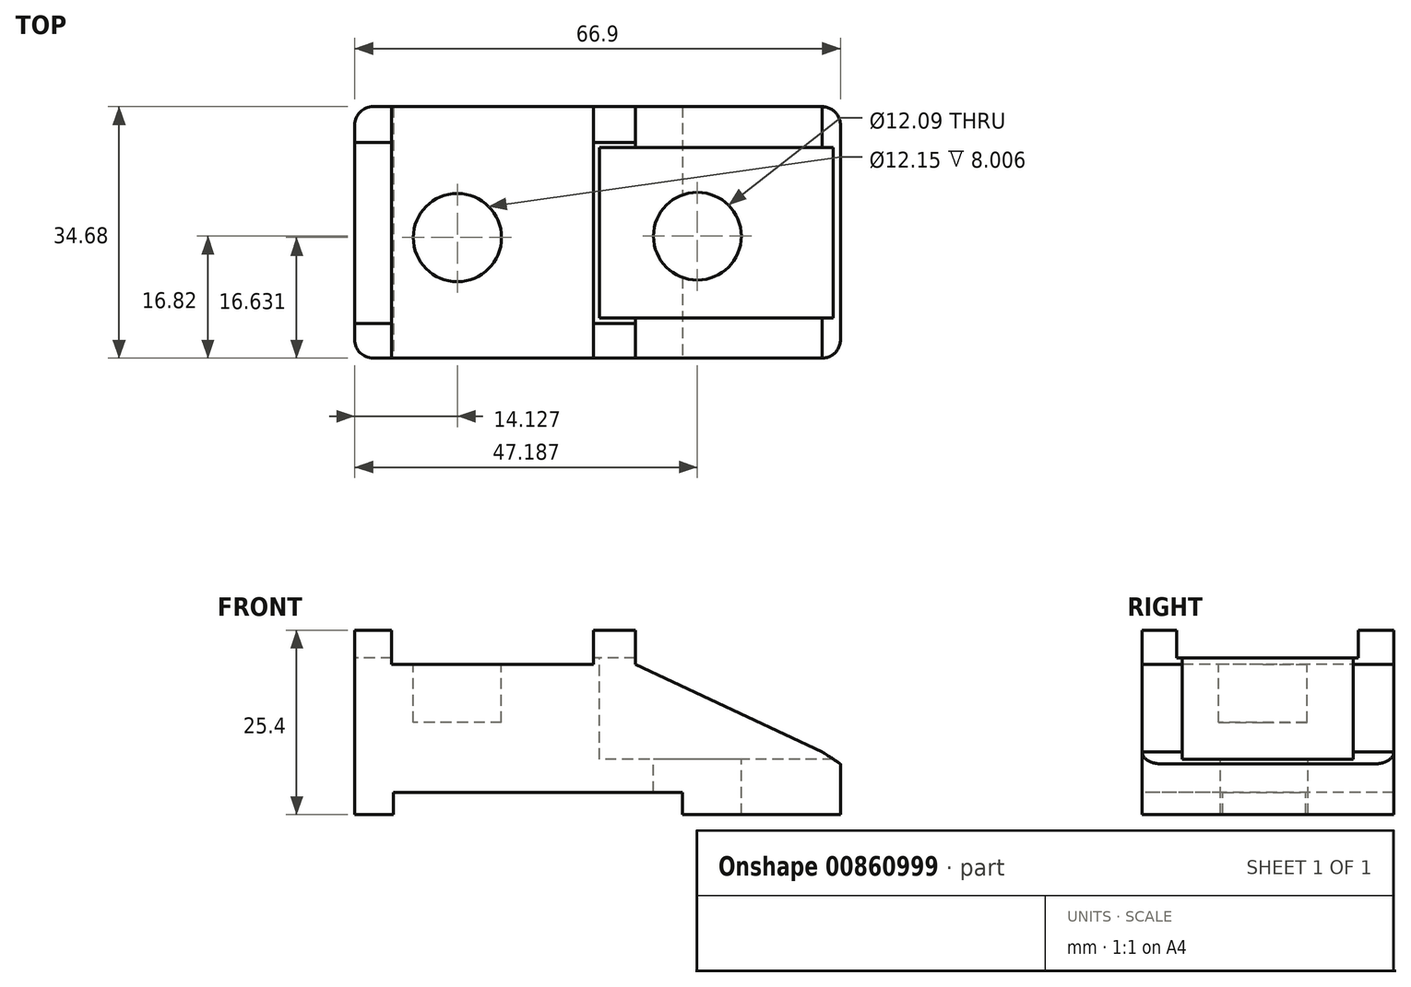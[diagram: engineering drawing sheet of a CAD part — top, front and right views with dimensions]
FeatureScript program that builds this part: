
annotation { "Feature Type Name" : "Feature", "Feature Type Description" : "" }
export const myFeature = defineFeature(function(context is Context, id is Id, definition is map)
    precondition{}
    {
        {
            var Q0;
            Q0=qCreatedBy(makeId("Top.planeOp"),FACE);
            var sketch = newSketch(context, id + "F0", { "sketchPlane" : qUnion([Q0])});
            skLineSegment(sketch, "E0.bottom", {"start": v(0, 0) * mm, "end": v(66.9, 0) * mm});
            skLineSegment(sketch, "E0.top", {"start": v(0, 34.68) * mm, "end": v(66.9, 34.68) * mm});
            skLineSegment(sketch, "E0.left", {"start": v(0, 0) * mm, "end": v(0, 34.68) * mm});
            skLineSegment(sketch, "E0.right", {"start": v(66.9, 0) * mm, "end": v(66.9, 34.68) * mm});
            skSolve(sketch);
        }
        {
            var Q0;
            Q0=makeQuery(id+"F0.imprint","IMPRINT",FACE,{"disambiguationData":[TD([[makeQuery(id+"F0.imprint","IMPRINT",EDGE,{"derivedFrom":sQuery(id+"F0.wireOp",EDGE,"E0.bottom")}),1.0]])]});
            extrude(context, id + "F1", {"entities" : qUnion([Q0]), "depth" : 25.4 * mm, "offsetDistance" : 25.4 * mm});
        }
        {
            var Q0;
            Q0=makeQuery(id+"F1.opExtrude","CAP_FACE",FACE,{"disambiguationData":[OSD([sQuery(id+"F0.wireOp",EDGE,"E0.bottom"),sQuery(id+"F0.wireOp",EDGE,"E0.top"),sQuery(id+"F0.wireOp",EDGE,"E0.left"),sQuery(id+"F0.wireOp",EDGE,"E0.right")])],"isStart":false});
            var sketch = newSketch(context, id + "F2", { "sketchPlane" : qUnion([Q0])});
            skCircle(sketch, "E1", {"center": v(47.19, 16.82) * mm, "radius": 6.05 * mm});
            skSolve(sketch);
        }
        {
            var Q0;
            Q0=makeQuery(id+"F2.imprint","IMPRINT",FACE,{"disambiguationData":[TD([[makeQuery(id+"F2.imprint","IMPRINT",EDGE,{"derivedFrom":sQuery(id+"F2.wireOp",EDGE,"E1")}),1.0]])]});
            extrude(context, id + "F3", {"entities" : qUnion([Q0]), "operationType" : NewBodyOperationType.REMOVE, "endBound" : BoundingType.THROUGH_ALL, "oppositeDirection" : true, "depth" : 25.4 * mm, "offsetDistance" : 25.4 * mm});
        }
        {
            var Q0;
            Q0=makeQuery(id+"F1.opExtrude","CAP_FACE",FACE,{"disambiguationData":[OSD([sQuery(id+"F0.wireOp",EDGE,"E0.bottom"),sQuery(id+"F0.wireOp",EDGE,"E0.top"),sQuery(id+"F0.wireOp",EDGE,"E0.left"),sQuery(id+"F0.wireOp",EDGE,"E0.right")])],"isStart":false});
            var sketch = newSketch(context, id + "F4", { "sketchPlane" : qUnion([Q0])});
            skCircle(sketch, "E2", {"center": v(14.13, 16.63) * mm, "radius": 6.08 * mm});
            skSolve(sketch);
        }
        {
            var Q0;
            Q0=makeQuery(id+"F4.imprint","IMPRINT",FACE,{"disambiguationData":[TD([[makeQuery(id+"F4.imprint","IMPRINT",EDGE,{"derivedFrom":sQuery(id+"F4.wireOp",EDGE,"E2")}),1.0]])]});
            extrude(context, id + "F5", {"entities" : qUnion([Q0]), "operationType" : NewBodyOperationType.REMOVE, "oppositeDirection" : true, "depth" : 12.7 * mm, "offsetDistance" : 25.4 * mm});
        }
        {
            var Q0;
            Q0=makeQuery(id+"F1.opExtrude","CAP_FACE",FACE,{"disambiguationData":[OSD([sQuery(id+"F0.wireOp",EDGE,"E0.bottom"),sQuery(id+"F0.wireOp",EDGE,"E0.top"),sQuery(id+"F0.wireOp",EDGE,"E0.left"),sQuery(id+"F0.wireOp",EDGE,"E0.right")])],"isStart":false});
            var sketch = newSketch(context, id + "F6", { "sketchPlane" : qUnion([Q0])});
            skLineSegment(sketch, "E3.bottom", {"start": v(66.9, 29.05) * mm, "end": v(33.67, 29.05) * mm});
            skLineSegment(sketch, "E3.top", {"start": v(66.9, 5.54) * mm, "end": v(33.67, 5.54) * mm});
            skLineSegment(sketch, "E3.left", {"start": v(66.9, 29.05) * mm, "end": v(66.9, 5.54) * mm});
            skLineSegment(sketch, "E3.right", {"start": v(33.67, 29.05) * mm, "end": v(33.67, 5.54) * mm});
            skSolve(sketch);
        }
        {
            var Q0;
            Q0=makeQuery(id+"F6.imprint","IMPRINT",FACE,{"disambiguationData":[TD([[makeQuery(id+"F6.imprint","IMPRINT",EDGE,{"derivedFrom":sQuery(id+"F6.wireOp",EDGE,"E3.bottom")}),1.0]])]});
            extrude(context, id + "F7", {"entities" : qUnion([Q0]), "operationType" : NewBodyOperationType.REMOVE, "oppositeDirection" : true, "depth" : 17.78 * mm, "offsetDistance" : 25.4 * mm});
        }
        {
            var Q0;
            Q0=makeQuery(id+"F1.opExtrude","SWEPT_FACE",FACE,{"disambiguationData":[OSD([sQuery(id+"F0.wireOp",EDGE,"E0.bottom")])]});
            var sketch = newSketch(context, id + "F8", { "sketchPlane" : qUnion([Q0])});
            skLineSegment(sketch, "E4.bottom", {"start": v(5.07, 25.4) * mm, "end": v(32.85, 25.4) * mm});
            skLineSegment(sketch, "E4.top", {"start": v(5.07, 20.7) * mm, "end": v(32.85, 20.7) * mm});
            skLineSegment(sketch, "E4.left", {"start": v(5.07, 25.4) * mm, "end": v(5.07, 20.7) * mm});
            skLineSegment(sketch, "E4.right", {"start": v(32.85, 25.4) * mm, "end": v(32.85, 20.7) * mm});
            skLineSegment(sketch, "E5.bottom", {"start": v(9.54, 20.7) * mm, "end": v(28.6, 20.7) * mm});
            skLineSegment(sketch, "E5.top", {"start": v(9.54, 16.57) * mm, "end": v(28.6, 16.57) * mm});
            skLineSegment(sketch, "E5.left", {"start": v(9.54, 20.7) * mm, "end": v(9.54, 16.57) * mm});
            skLineSegment(sketch, "E5.right", {"start": v(28.6, 20.7) * mm, "end": v(28.6, 16.57) * mm});
            skLineSegment(sketch, "E6.bottom", {"start": v(5.29, 0) * mm, "end": v(45.16, 0) * mm});
            skLineSegment(sketch, "E6.top", {"start": v(5.29, 3.06) * mm, "end": v(45.16, 3.06) * mm});
            skLineSegment(sketch, "E6.left", {"start": v(5.29, 0) * mm, "end": v(5.29, 3.06) * mm});
            skLineSegment(sketch, "E6.right", {"start": v(45.16, 0) * mm, "end": v(45.16, 3.06) * mm});
            skLineSegment(sketch, "E7", {"start": v(38.62, 25.4) * mm, "end": v(66.9, 6.98) * mm});
            skSolve(sketch);
        }
        {
            var Q0;
            Q0=makeQuery(id+"F8.imprint","IMPRINT",FACE,{"disambiguationData":[TD([[makeQuery(id+"F8.imprint","IMPRINT",EDGE,{"derivedFrom":sQuery(id+"F8.wireOp",EDGE,"E5.bottom")}),-1.0]])]});
            var Q1;
            Q1=makeQuery(id+"F8.imprint","IMPRINT",FACE,{"disambiguationData":[TD([[makeQuery(id+"F8.imprint","IMPRINT",EDGE,{"derivedFrom":sQuery(id+"F8.wireOp",EDGE,"E4.bottom")}),-1.0]])]});
            var Q2;
            {var subQ0=sQuery(id+"F8.wireOp",EDGE,"E7");Q2=makeQuery(id+"F8.imprint","IMPRINT",FACE,{"disambiguationData":[TD([[makeQuery(id+"F8.imprint","IMPRINT",EDGE,{"derivedFrom":subQ0}),1.0]])]});}
            var Q3;
            Q3=makeQuery(id+"F8.imprint","IMPRINT",FACE,{"disambiguationData":[TD([[makeQuery(id+"F8.imprint","IMPRINT",EDGE,{"derivedFrom":sQuery(id+"F8.wireOp",EDGE,"E6.bottom")}),1.0]])]});
            extrude(context, id + "F9", {"entities" : qUnion([Q0, Q1, Q2, Q3]), "operationType" : NewBodyOperationType.REMOVE, "endBound" : BoundingType.THROUGH_ALL, "oppositeDirection" : true, "depth" : 25.4 * mm, "offsetDistance" : 25.4 * mm});
        }
        {
            var Q0;
            Q0=makeQuery(id+"F1.opExtrude","SWEPT_FACE",FACE,{"disambiguationData":[OSD([sQuery(id+"F0.wireOp",EDGE,"E0.left")])]});
            var sketch = newSketch(context, id + "F10", { "sketchPlane" : qUnion([Q0])});
            skLineSegment(sketch, "E8.bottom", {"start": v(-29.76, 25.4) * mm, "end": v(-4.76, 25.4) * mm});
            skLineSegment(sketch, "E8.top", {"start": v(-29.76, 21.6) * mm, "end": v(-4.76, 21.6) * mm});
            skLineSegment(sketch, "E8.left", {"start": v(-29.76, 25.4) * mm, "end": v(-29.76, 21.6) * mm});
            skLineSegment(sketch, "E8.right", {"start": v(-4.76, 25.4) * mm, "end": v(-4.76, 21.6) * mm});
            skLineSegment(sketch, "E9.bottom", {"start": v(-25.94, 21.6) * mm, "end": v(-8.43, 21.6) * mm});
            skLineSegment(sketch, "E9.top", {"start": v(-25.94, 18.07) * mm, "end": v(-8.43, 18.07) * mm});
            skLineSegment(sketch, "E9.left", {"start": v(-25.94, 21.6) * mm, "end": v(-25.94, 18.07) * mm});
            skLineSegment(sketch, "E9.right", {"start": v(-8.43, 21.6) * mm, "end": v(-8.43, 18.07) * mm});
            skSolve(sketch);
        }
        {
            var Q0;
            Q0=makeQuery(id+"F10.imprint","IMPRINT",FACE,{"disambiguationData":[TD([[makeQuery(id+"F10.imprint","IMPRINT",EDGE,{"derivedFrom":sQuery(id+"F10.wireOp",EDGE,"E8.bottom")}),1.0]])]});
            var Q1;
            Q1=makeQuery(id+"F10.imprint","IMPRINT",FACE,{"disambiguationData":[TD([[makeQuery(id+"F10.imprint","IMPRINT",EDGE,{"derivedFrom":sQuery(id+"F10.wireOp",EDGE,"E9.bottom")}),-1.0]])]});
            extrude(context, id + "F11", {"entities" : qUnion([Q0, Q1]), "operationType" : NewBodyOperationType.REMOVE, "endBound" : BoundingType.THROUGH_ALL, "oppositeDirection" : true, "depth" : 25.4 * mm, "offsetDistance" : 25.4 * mm});
        }
        {
            var Q0;
            Q0=makeQuery(id+"F1.opExtrude","SWEPT_EDGE",EDGE,{"disambiguationData":[OSD([sQuery(id+"F0.wireOp",EDGE,"E0.bottom"),sQuery(id+"F0.wireOp",EDGE,"E0.right")])]});
            var Q1;
            Q1=makeQuery(id+"F1.opExtrude","SWEPT_EDGE",EDGE,{"disambiguationData":[OSD([sQuery(id+"F0.wireOp",EDGE,"E0.top"),sQuery(id+"F0.wireOp",EDGE,"E0.right")])]});
            fillet(context, id + "F12", {"entities" : qUnion([Q0, Q1]), "radius" : 2.54 * mm, "tangentPropagation" : true, "allowEdgeOverflow" : false});
        }
        {
            var Q0;
            Q0=makeQuery(id+"F1.opExtrude","SWEPT_EDGE",EDGE,{"disambiguationData":[OSD([sQuery(id+"F0.wireOp",EDGE,"E0.top"),sQuery(id+"F0.wireOp",EDGE,"E0.left")])]});
            var Q1;
            Q1=makeQuery(id+"F1.opExtrude","SWEPT_EDGE",EDGE,{"disambiguationData":[OSD([sQuery(id+"F0.wireOp",EDGE,"E0.bottom"),sQuery(id+"F0.wireOp",EDGE,"E0.left")])]});
            fillet(context, id + "F13", {"entities" : qUnion([Q0, Q1]), "radius" : 2.54 * mm, "tangentPropagation" : true, "allowEdgeOverflow" : false});
        }
        {
            var Q0;
            Q0=makeQuery(id+"F1.opExtrude","SWEPT_FACE",FACE,{"disambiguationData":[OSD([sQuery(id+"F0.wireOp",EDGE,"E0.bottom")])]});
            var sketch = newSketch(context, id + "F14", { "sketchPlane" : qUnion([Q0])});
            skLineSegment(sketch, "E10", {"start": v(38.62, 25.4) * mm, "end": v(38.62, 20.7) * mm});
            skLineSegment(sketch, "E11", {"start": v(38.62, 20.7) * mm, "end": v(64.36, 8.64) * mm});
            skSolve(sketch);
        }
        {
            var Q0;
            Q0=makeQuery(id+"F14.imprint","IMPRINT",FACE,{"disambiguationData":[TD([[makeQuery(id+"F14.imprint","IMPRINT",EDGE,{"derivedFrom":sQuery(id+"F14.wireOp",EDGE,"E10")}),1.0]])]});
            extrude(context, id + "F15", {"entities" : qUnion([Q0]), "operationType" : NewBodyOperationType.REMOVE, "endBound" : BoundingType.THROUGH_ALL, "oppositeDirection" : true, "depth" : 25.4 * mm, "offsetDistance" : 25.4 * mm});
        }
    });
